# Revit family: QF_BOURGEAT_Chariots_pour_transport_Assiettes
name_source: partatom
category: Equipement spécialisé
revit_build: Autodesk Revit 2015 (Build: 20140606_1530(x64)
units: mm (PartAtom-declared; Revit-internal decimal feet)

## types (12) — shared parameters
Barre renfort longueur = 987 mm  [stored 3.23819 ft]
Certification = NF Hygiène Alimentaire
Charge max = 200.00 kg
Charge maximale = 200 Kg
Fabricant = BOURGEAT
Longueur hors tout = 1112 mm  [stored 3.64829 ft]
Longueur support = 1032 mm
Spécification du Fabricant = Chariots à assiettes
URL catalogue = http://www.bourgeat.fr

## per-type parameters (varying)
| type | Barre de renfort | Barre renfort largeur | Decal séparation bas | Hauteur echelle | Hauteur hors tout | Hauteur support | Hauteur séparation | Largeur séparation | Modèle | Profondeur echelle | Profondeur hors tout | arceau_petite_vaisselle | arceau_standard | pare_chute_ramequin_grand_modele | pare_chute_ramequin_petit_modele | séparation_standard |
| Chariot assiettes standard - Petit modèle - sans séparation | Non | 415 mm  [stored 1.36155 ft] | 133 mm  [stored 0.436352 ft] | 622 mm  [stored 2.04068 ft] | 785 mm | 498 mm  [stored 1.63386 ft] | 531 mm  [stored 1.74213 ft] | 280 mm  [stored 0.918635 ft] | 791006 | 465 mm  [stored 1.52559 ft] | 540 mm  [stored 1.77165 ft] | Non | Oui | Non | Non | Non |
| Chariot assiettes standard - Grand modèle - sans séparation | Non | 502 mm  [stored 1.64698 ft] | 192 mm  [stored 0.629921 ft] | 622 mm  [stored 2.04068 ft] | 785 mm | 458 mm | 488 mm  [stored 1.60105 ft] | 435 mm  [stored 1.42717 ft] | 792006 | 552 mm  [stored 1.81102 ft] | 627 mm  [stored 2.05709 ft] | Non | Oui | Non | Non | Non |
| Chariot assiettes standard - Petit modèle - avec 2 séparations | Non | 415 mm  [stored 1.36155 ft] | 133 mm  [stored 0.436352 ft] | 622 mm  [stored 2.04068 ft] | 785 mm | 498 mm  [stored 1.63386 ft] | 531 mm  [stored 1.74213 ft] | 280 mm  [stored 0.918635 ft] | 791206 | 465 mm  [stored 1.52559 ft] | 540 mm  [stored 1.77165 ft] | Non | Oui | Non | Non | Oui |
| Chariot assiettes standard - Grand modèle - avec 2 séparations | Non | 502 mm  [stored 1.64698 ft] | 192 mm  [stored 0.629921 ft] | 622 mm  [stored 2.04068 ft] | 785 mm | 458 mm | 488 mm  [stored 1.60105 ft] | 435 mm  [stored 1.42717 ft] | 792206 | 552 mm  [stored 1.81102 ft] | 627 mm  [stored 2.05709 ft] | Non | Oui | Non | Non | Oui |
| Chariot assiettes réhaussé - Petit modèle - sans séparation | Oui | 415 mm  [stored 1.36155 ft] | 446 mm  [stored 1.46325 ft] | 935 mm  [stored 3.06759 ft] | 1098 mm  [stored 3.60236 ft] | 498 mm  [stored 1.63386 ft] | 531 mm  [stored 1.74213 ft] | 280 mm  [stored 0.918635 ft] | 791106 | 465 mm  [stored 1.52559 ft] | 540 mm  [stored 1.77165 ft] | Non | Oui | Non | Non | Non |
| Chariot assiettes réhaussé - Petit modèle - avec 2 séparations | Oui | 415 mm  [stored 1.36155 ft] | 446 mm  [stored 1.46325 ft] | 935 mm  [stored 3.06759 ft] | 1098 mm  [stored 3.60236 ft] | 498 mm  [stored 1.63386 ft] | 531 mm  [stored 1.74213 ft] | 280 mm  [stored 0.918635 ft] | 791306 | 465 mm  [stored 1.52559 ft] | 540 mm  [stored 1.77165 ft] | Non | Oui | Non | Non | Oui |
| Chariot assiettes réhaussé - Grand modèle - sans séparation | Oui | 502 mm  [stored 1.64698 ft] | 446 mm  [stored 1.46325 ft] | 935 mm  [stored 3.06759 ft] | 1098 mm  [stored 3.60236 ft] | 498 mm  [stored 1.63386 ft] | 531 mm  [stored 1.74213 ft] | 435 mm  [stored 1.42717 ft] | 792106 | 552 mm  [stored 1.81102 ft] | 627 mm  [stored 2.05709 ft] | Non | Oui | Non | Non | Non |
| Chariot assiettes réhaussé - Grand modèle - avec 2 séparations | Oui | 502 mm  [stored 1.64698 ft] | 446 mm  [stored 1.46325 ft] | 935 mm  [stored 3.06759 ft] | 1098 mm  [stored 3.60236 ft] | 498 mm  [stored 1.63386 ft] | 531 mm  [stored 1.74213 ft] | 435 mm  [stored 1.42717 ft] | 792306 | 552 mm  [stored 1.81102 ft] | 627 mm  [stored 2.05709 ft] | Non | Oui | Non | Non | Oui |
| Chariot petite vaisselle réhaussé - Grand modèle - avec 2 séparations | Oui | 502 mm  [stored 1.64698 ft] | 446 mm  [stored 1.46325 ft] | 935 mm  [stored 3.06759 ft] | 1098 mm  [stored 3.60236 ft] | 498 mm  [stored 1.63386 ft] | 531 mm  [stored 1.74213 ft] | 435 mm  [stored 1.42717 ft] | 792306+792904 | 552 mm  [stored 1.81102 ft] | 627 mm  [stored 2.05709 ft] | Oui | Non | Oui | Non | Non |
| Chariot petite vaisselle réhaussé - Petit modèle - avec 2 séparations | Oui | 415 mm  [stored 1.36155 ft] | 446 mm  [stored 1.46325 ft] | 935 mm  [stored 3.06759 ft] | 1098 mm  [stored 3.60236 ft] | 498 mm  [stored 1.63386 ft] | 531 mm  [stored 1.74213 ft] | 280 mm  [stored 0.918635 ft] | 791306+791904 | 465 mm  [stored 1.52559 ft] | 540 mm  [stored 1.77165 ft] | Oui | Non | Non | Oui | Non |
| Chariot petite vaisselle standard - Grand modèle - avec 2 séparations | Non | 502 mm  [stored 1.64698 ft] | 192 mm  [stored 0.629921 ft] | 622 mm  [stored 2.04068 ft] | 785 mm | 458 mm | 488 mm  [stored 1.60105 ft] | 435 mm  [stored 1.42717 ft] | 792206+792904 | 552 mm  [stored 1.81102 ft] | 627 mm  [stored 2.05709 ft] | Oui | Non | Oui | Non | Non |
| Chariot petite vaisselle standard - Petit modèle - avec 2 séparations | Non | 415 mm  [stored 1.36155 ft] | 133 mm  [stored 0.436352 ft] | 622 mm  [stored 2.04068 ft] | 785 mm | 498 mm  [stored 1.63386 ft] | 531 mm  [stored 1.74213 ft] | 280 mm  [stored 0.918635 ft] | 791206+791904 | 465 mm  [stored 1.52559 ft] | 540 mm  [stored 1.77165 ft] | Oui | Non | Non | Oui | Non |

note: [stored X ft] marks values corroborated as IEEE doubles in the binary element streams (Revit-internal decimal feet)

## geometry (parser evidence)
native form markers: Blend x12
no freeform markers — native parametric forms only
